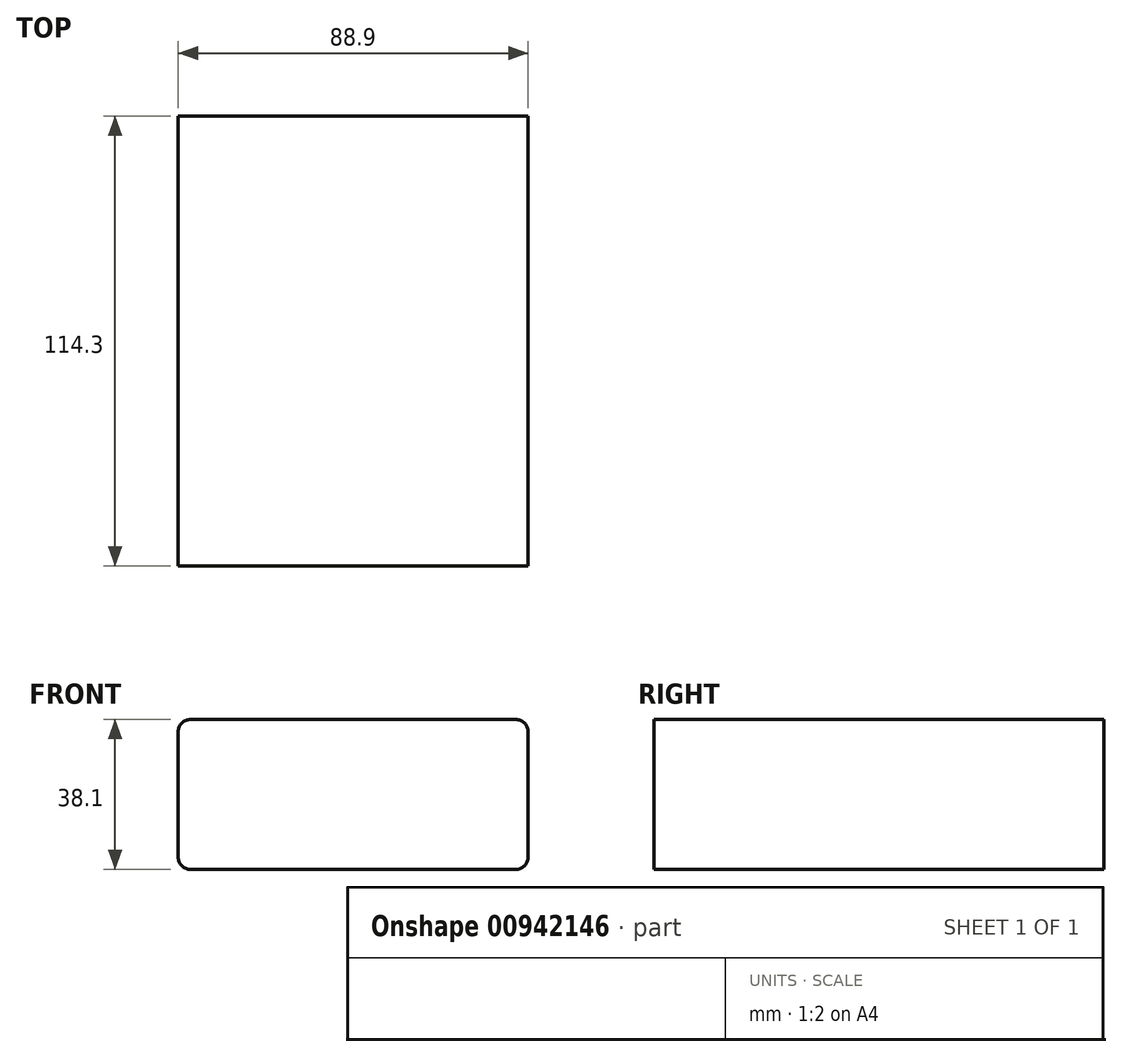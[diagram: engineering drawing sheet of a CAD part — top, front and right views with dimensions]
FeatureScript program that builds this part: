
annotation { "Feature Type Name" : "Feature", "Feature Type Description" : "" }
export const myFeature = defineFeature(function(context is Context, id is Id, definition is map)
    precondition{}
    {
        {
            var Q0;
            Q0=qCreatedBy(makeId("Front.planeOp"),FACE);
            var sketch = newSketch(context, id + "F0", { "sketchPlane" : qUnion([Q0])});
            skLineSegment(sketch, "E0.bottom", {"start": v(41.28, 19.05) * mm, "end": v(-41.28, 19.05) * mm});
            skLineSegment(sketch, "E0.top", {"start": v(41.28, -19.05) * mm, "end": v(-41.28, -19.05) * mm});
            skLineSegment(sketch, "E0.left", {"start": v(44.45, 15.87) * mm, "end": v(44.45, -15.88) * mm});
            skLineSegment(sketch, "E0.right", {"start": v(-44.45, 15.87) * mm, "end": v(-44.45, -15.88) * mm});
            skPoint(sketch, "E0.middle", {"position": v(0, 0) * mm});
            skPoint(sketch, "E1.visualSharp", {"position": v(-44.45, 19.05) * mm});
            skArc(sketch, "E1.filletArc", {"start": v(-41.28, 19.05) * mm, "mid": v(-43.52, 18.12) * mm, "end": v(-44.45, 15.87) * mm});
            skPoint(sketch, "E2.visualSharp", {"position": v(-44.45, -19.05) * mm});
            skArc(sketch, "E2.filletArc", {"start": v(-44.45, -15.88) * mm, "mid": v(-43.52, -18.12) * mm, "end": v(-41.28, -19.05) * mm});
            skPoint(sketch, "E3.visualSharp", {"position": v(44.45, -19.05) * mm});
            skArc(sketch, "E3.filletArc", {"start": v(41.28, -19.05) * mm, "mid": v(43.52, -18.12) * mm, "end": v(44.45, -15.88) * mm});
            skPoint(sketch, "E4.visualSharp", {"position": v(44.45, 19.05) * mm});
            skArc(sketch, "E4.filletArc", {"start": v(44.45, 15.87) * mm, "mid": v(43.52, 18.12) * mm, "end": v(41.28, 19.05) * mm});
            skSolve(sketch);
        }
        {
            var Q0;
            Q0 = qSketchRegion(id + "F0", true);
            extrude(context, id + "F1", {"entities" : qUnion([Q0]), "endBound" : BoundingType.SYMMETRIC, "depth" : 114.3 * mm, "offsetDistance" : 25 * mm});
        }
    });
